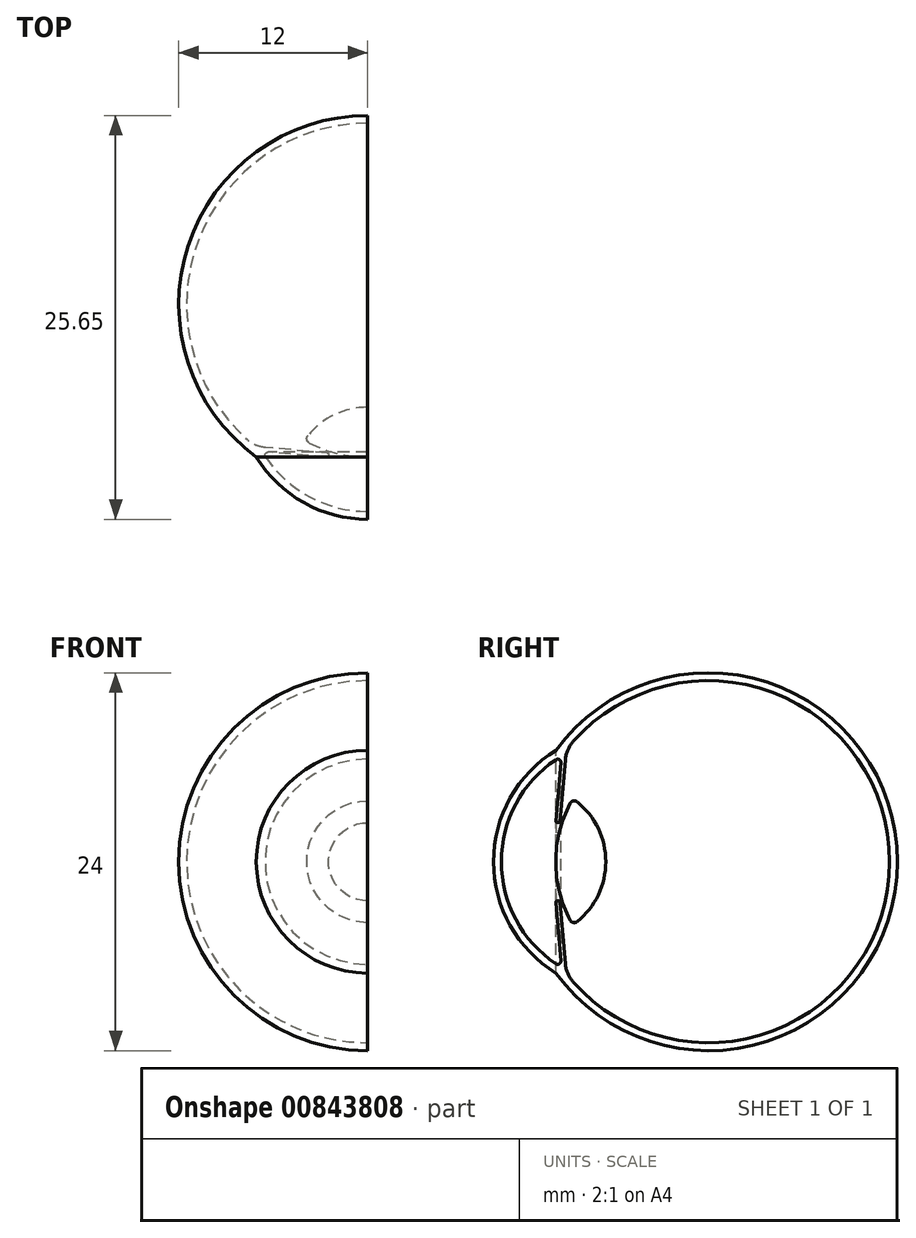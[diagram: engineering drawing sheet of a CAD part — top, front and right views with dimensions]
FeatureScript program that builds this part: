
annotation { "Feature Type Name" : "Feature", "Feature Type Description" : "" }
export const myFeature = defineFeature(function(context is Context, id is Id, definition is map)
    precondition{}
    {
        {
            var Q0;
            Q0=qCreatedBy(makeId("Right.planeOp"),FACE);
            var sketch = newSketch(context, id + "F0", { "sketchPlane" : qUnion([Q0])});
            skArc(sketch, "E0", {"start": v(-9.7, 6.48) * mm, "mid": v(-12.23, 3.67) * mm, "end": v(-13.15, 0) * mm});
            skArc(sketch, "E1", {"start": v(11.5, 0) * mm, "mid": v(4.09, 10.75) * mm, "end": v(-8.6, 7.64) * mm});
            skLineSegment(sketch, "E2", {"start": v(11.5, 0) * mm, "end": v(-9.7, 0) * mm});
            skLineSegment(sketch, "E3", {"start": v(-9.7, 0) * mm, "end": v(-13.15, 0) * mm});
            skLineSegment(sketch, "E4", {"start": v(-9.7, 0) * mm, "end": v(-9.7, 2.5) * mm, "construction": true});
            skLineSegment(sketch, "E5", {"start": v(-9.7, 2.6) * mm, "end": v(-9.38, 6.3) * mm});
            skArc(sketch, "E6.0", {"start": v(-9.7, 7.08) * mm, "mid": v(-12.6, 4.05) * mm, "end": v(-13.65, 0) * mm});
            skArc(sketch, "E6.1", {"start": v(12, 0) * mm, "mid": v(3.72, 11.4) * mm, "end": v(-9.7, 7.08) * mm});
            skLineSegment(sketch, "E7", {"start": v(11.5, 0) * mm, "end": v(12, 0) * mm});
            skLineSegment(sketch, "E8", {"start": v(-13.65, 0) * mm, "end": v(-13.15, 0) * mm});
            skArc(sketch, "E9", {"start": v(-9.7, 0) * mm, "mid": v(-9.47, 1.9) * mm, "end": v(-8.8, 3.7) * mm});
            skArc(sketch, "E10", {"start": v(-6.53, 0) * mm, "mid": v(-7, 2.1) * mm, "end": v(-8.34, 3.8) * mm});
            skPoint(sketch, "E11.visualSharp", {"position": v(-8.62, 4.02) * mm});
            skArc(sketch, "E11.filletArc", {"start": v(-8.34, 3.8) * mm, "mid": v(-8.59, 3.86) * mm, "end": v(-8.8, 3.7) * mm});
            skLineSegment(sketch, "E12", {"start": v(-9.6, 2.5) * mm, "end": v(-9.54, 2.49) * mm});
            skLineSegment(sketch, "E13", {"start": v(-9.43, 2.58) * mm, "end": v(-9.1, 6.48) * mm});
            skPoint(sketch, "E14.0.visualSharp", {"position": v(-9.35, 6.7) * mm});
            skArc(sketch, "E14.0.filletArc", {"start": v(-9.38, 6.3) * mm, "mid": v(-9.48, 6.49) * mm, "end": v(-9.7, 6.48) * mm});
            skArc(sketch, "E15.0.filletArc", {"start": v(-8.6, 7.64) * mm, "mid": v(-8.94, 7.1) * mm, "end": v(-9.1, 6.48) * mm});
            skPoint(sketch, "E16.0.visualSharp", {"position": v(-9.44, 2.48) * mm});
            skArc(sketch, "E16.0.filletArc", {"start": v(-9.54, 2.49) * mm, "mid": v(-9.46, 2.5) * mm, "end": v(-9.43, 2.58) * mm});
            skPoint(sketch, "E17.0.visualSharp", {"position": v(-9.7, 2.5) * mm});
            skArc(sketch, "E17.0.filletArc", {"start": v(-9.7, 2.6) * mm, "mid": v(-9.67, 2.53) * mm, "end": v(-9.6, 2.5) * mm});
            skSolve(sketch);
        }
        {
            var Q0;
            Q0=makeQuery(id+"F0.imprint","IMPRINT",FACE,{"disambiguationData":[TD([[makeQuery(id+"F0.imprint","IMPRINT",EDGE,{"derivedFrom":sQuery(id+"F0.wireOp",EDGE,"E0")}),-1.0]])]});
            var Q1;
            {var subQ0=sQuery(id+"F0.wireOp",EDGE,"E5");Q1=makeQuery(id+"F0.imprint","IMPRINT",FACE,{"disambiguationData":[TD([[makeQuery(id+"F0.imprint","IMPRINT",EDGE,{"derivedFrom":subQ0}),-1.0]])]});}
            var Q2;
            Q2=sQuery(id+"F0.wireOp",EDGE,"E2");
            revolve(context, id + "F1", {"surfaceOperationType" : NewSurfaceOperationType.NEW, "entities" : qUnion([Q0, Q1]), "axis" : qUnion([Q2]), "revolveType" : RevolveType.ONE_DIRECTION, "angle" : 180 * degree});
        }
        {
            var Q0;
            {var subQ0=sQuery(id+"F0.wireOp",EDGE,"E9");Q0=makeQuery(id+"F0.imprint","IMPRINT",FACE,{"disambiguationData":[TD([[makeQuery(id+"F0.imprint","IMPRINT",EDGE,{"derivedFrom":subQ0}),-1.0]])]});}
            var Q1;
            Q1=sQuery(id+"F0.wireOp",EDGE,"E2");
            revolve(context, id + "F2", {"surfaceOperationType" : NewSurfaceOperationType.NEW, "entities" : qUnion([Q0]), "axis" : qUnion([Q1]), "revolveType" : RevolveType.ONE_DIRECTION, "angle" : 180 * degree});
        }
    });
